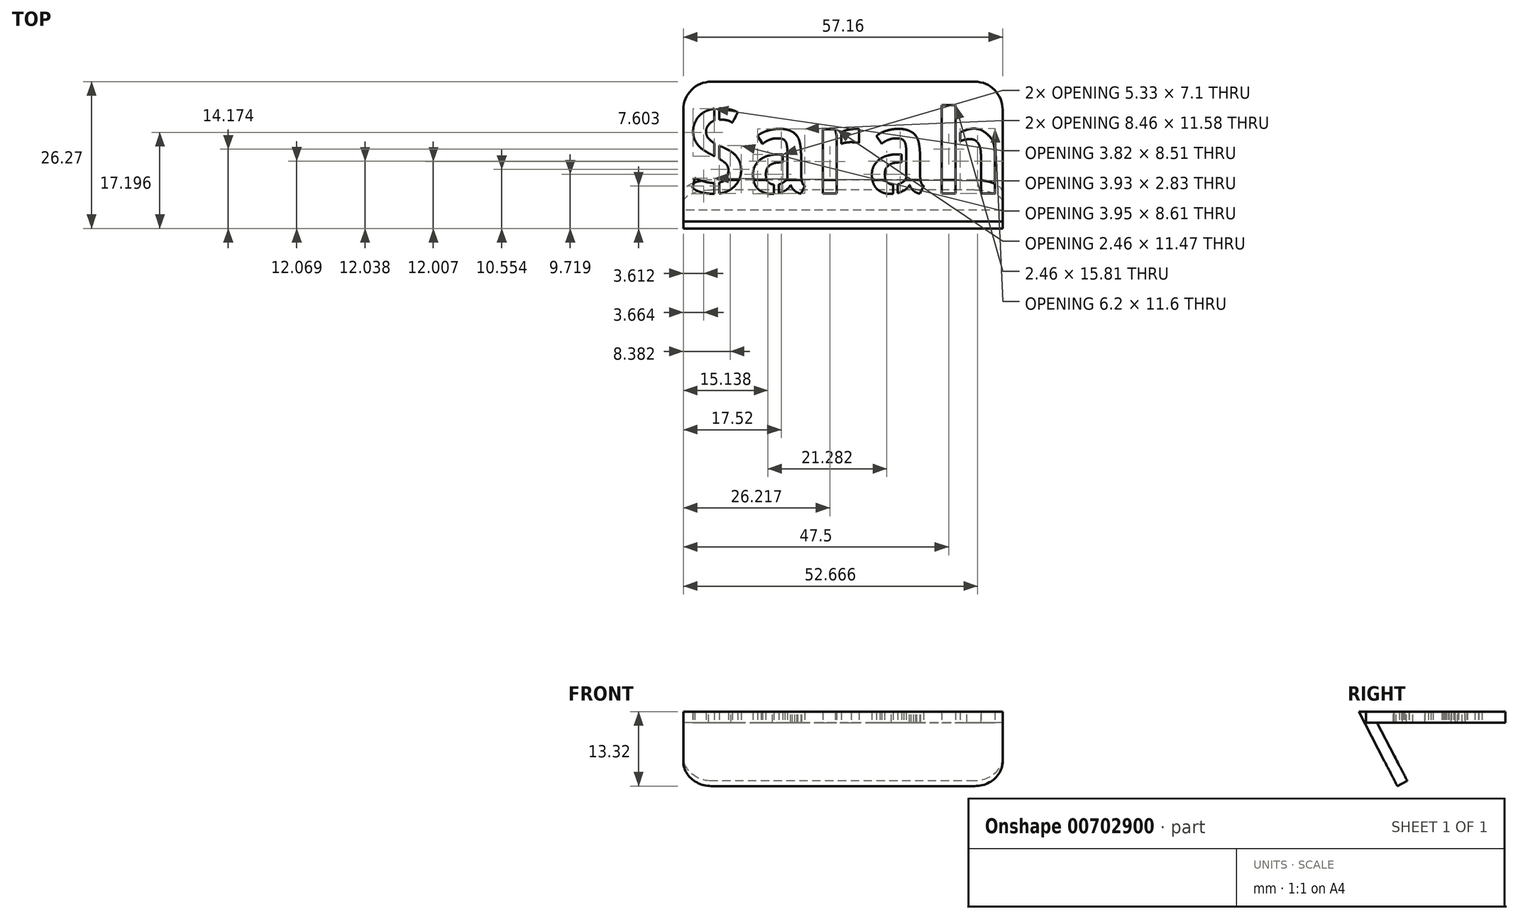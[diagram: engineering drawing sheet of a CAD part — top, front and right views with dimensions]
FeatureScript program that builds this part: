
annotation { "Feature Type Name" : "Feature", "Feature Type Description" : "" }
export const myFeature = defineFeature(function(context is Context, id is Id, definition is map)
    precondition{}
    {
        {
            var Q0;
            Q0=qCreatedBy(makeId("Top.planeOp"),FACE);
            var sketch = newSketch(context, id + "F0", { "sketchPlane" : qUnion([Q0])});
            skLineSegment(sketch, "E0.bottom", {"start": v(-23.58, 12.5) * mm, "end": v(33.58, 12.5) * mm});
            skLineSegment(sketch, "E0.top", {"start": v(-23.58, -12.5) * mm, "end": v(33.58, -12.5) * mm});
            skLineSegment(sketch, "E0.left", {"start": v(-23.58, 12.5) * mm, "end": v(-23.58, -12.5) * mm});
            skLineSegment(sketch, "E0.right", {"start": v(33.58, 12.5) * mm, "end": v(33.58, -12.5) * mm});
            skText(sketch, "E1", { "text": "Sarah", "fontName": "AllertaStencil-Regular.ttf"});
            const initialGuessF0  = {"E1": [-0.02358, -0.0075, 1, 0, 0.015]};
            skSetInitialGuess(sketch, initialGuessF0);
            skSolve(sketch);
        }
        {
            var Q0;
            Q0=makeQuery(id+"F0.imprint","IMPRINT",FACE,{"disambiguationData":[TD([[makeQuery(id+"F0.imprint","IMPRINT",EDGE,{"derivedFrom":sQuery(id+"F0.wireOp",EDGE,"E0.bottom")}),-1.0]])]});
            extrude(context, id + "F1", {"entities" : qUnion([Q0]), "depth" : 2 * mm, "offsetDistance" : 25 * mm});
        }
        {
            var Q0;
            {var subQ0=sQuery(id+"F0.wireOp",EDGE,"E0.left");Q0=makeQuery(id+"FYEOEdhl7jzHk82_2.opBoolean","MERGE",FACE,{"derivedFrom":[makeQuery(id+"F1.opExtrude","SWEPT_FACE",FACE,{"disambiguationData":[OSD([subQ0])]}),makeQuery(id+"FOv1BJgTRWeWuMw_1.opExtrude","CAP_FACE",FACE,{"disambiguationData":[OSD([sQuery(id+"F0.wireOp",EDGE,"E0.bottom"),subQ0,sQuery(id+"Fjco5yBOxZZxTCI_1.wireOp",EDGE,"TpTMtmOo-qoIM-rLEy-p7IH-mKgsBanMGF23"),sQuery(id+"Fjco5yBOxZZxTCI_1.wireOp",EDGE,"Ja6BvVoQ-cpFi-Lcom-cL8s-5xC4kZiynyNl"),sQuery(id+"Fjco5yBOxZZxTCI_1.wireOp",EDGE,"utNyaJ8P-FD6r-AD7x-tpFW-fHytfVhziHLl"),sQuery(id+"Fjco5yBOxZZxTCI_1.wireOp",EDGE,"xGzW29bi-H5H8-ObLh-gdKj-mSPkAtMAUUzO")])],"isStart":true})]});}
            var sketch = newSketch(context, id + "F2", { "sketchPlane" : qUnion([Q0])});
            skLineSegment(sketch, "E2", {"start": v(11.52, 2) * mm, "end": v(5.09, -10.4) * mm});
            skLineSegment(sketch, "E3", {"start": v(5.09, -10.4) * mm, "end": v(6.87, -11.32) * mm});
            skLineSegment(sketch, "E4", {"start": v(6.87, -11.32) * mm, "end": v(13.77, 2) * mm});
            skLineSegment(sketch, "E5", {"start": v(13.77, 2) * mm, "end": v(11.52, 2) * mm});
            skSolve(sketch);
        }
        {
            var Q0;
            {var subQ4=sQuery(id+"F2.wireOp",EDGE,"E3");Q0=makeQuery(id+"F2.imprint","IMPRINT",FACE,{"disambiguationData":[TD([[makeQuery(id+"F2.imprint","IMPRINT",EDGE,{"derivedFrom":subQ4}),1.0]])]});}
            var Q1;
            Q1=makeQuery(id+"F1.opExtrude","SWEPT_FACE",FACE,{"disambiguationData":[OSD([sQuery(id+"F0.wireOp",EDGE,"E0.right")])]});
            extrude(context, id + "F3", {"entities" : qUnion([Q0]), "endBound" : BoundingType.UP_TO_SURFACE, "oppositeDirection" : true, "depth" : 75 * mm, "endBoundEntityFace" : qUnion([Q1]), "offsetDistance" : 25 * mm});
        }
        {
            var Q0;
            Q0=makeQuery(id+"F1.opExtrude","SWEPT_EDGE",EDGE,{"disambiguationData":[OSD([sQuery(id+"F0.wireOp",EDGE,"E0.bottom"),sQuery(id+"F0.wireOp",EDGE,"E0.left")])]});
            var Q1;
            Q1=makeQuery(id+"F1.opExtrude","SWEPT_EDGE",EDGE,{"disambiguationData":[OSD([sQuery(id+"F0.wireOp",EDGE,"E0.bottom"),sQuery(id+"F0.wireOp",EDGE,"E0.right")])]});
            var Q2;
            Q2=makeQuery(id+"F3.opExtrude","CAP_EDGE",EDGE,{"disambiguationData":[OSD([sQuery(id+"F2.wireOp",EDGE,"E3")])],"isStart":false});
            var Q3;
            Q3=makeQuery(id+"F3.opExtrude","CAP_EDGE",EDGE,{"disambiguationData":[OSD([sQuery(id+"F2.wireOp",EDGE,"E3")])],"isStart":true});
            var Q4;
            Q4=makeQuery(id+"F3.opExtrude","TWEAK_EDGE",EDGE,{"derivedFrom":[makeQuery(id+"F1.opExtrude","SWEPT_FACE",FACE,{"disambiguationData":[OSD([sQuery(id+"F0.wireOp",EDGE,"E0.right")])]}),makeQuery(id+"F2.imprint","IMPRINT",EDGE,{"derivedFrom":sQuery(id+"F2.wireOp",EDGE,"E3")})]});
            fillet(context, id + "F4", {"entities" : qUnion([Q0, Q1, Q2, Q3, Q4]), "radius" : 5 * mm, "tangentPropagation" : true, "allowEdgeOverflow" : false});
        }
    });
